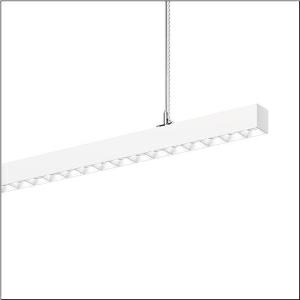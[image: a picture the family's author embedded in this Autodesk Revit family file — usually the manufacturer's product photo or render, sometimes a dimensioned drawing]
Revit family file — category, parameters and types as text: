
# Revit family: silica_r__21_51mx37da47wb_26de
name_source: partatom
category: Lighting Fixtures
units: mm (PartAtom-declared; Revit-internal decimal feet)

## family parameters
Cut with Voids When Loaded = No
Host = Face
Light Source = No
Part Type = Normal
Room Calculation Point = No
Round Connector Dimension = Use Diameter
Shared = No

## types (1)
- --- (1 x LED, 7300 lm, 44 W, 4000K)
    Apparent Load = 44 VA
    CIE Flux Codes = 71 92 99 59 100
    Color Rendering = 80
    Color Temperature = 4000K
    Default Elevation = 1800 mm
    Description = Silica® 21, office luminaire, primary light control with darklight reflector, of PMMA, white, CAT 2 (L<= 3000cd/m²), light emission: direct/indirect distribution, primary light characteristic: asymmetric, installation type: suspended mounting, LED, rated luminous flux: 7.300lm, luminous efficacy: 166lm/W, light colour: 840, colour temperature: 4000K, control gear: DALI 2, with terminal, 3+2-pole, max. 2.5mm², mains connection: 220..240V, AC, 50/60Hz, rated input power: 44W, luminaire housing, of aluminium, traffic white (RAL 9016), length: 1.204mm, width: 53mm, height: 53mm, protection rating (complete): IP20, insulation class (complete): insulation class I (protective earthing), certification: CE, permissible operating ambient temperature: 0..+35°C, standard: EN 50419, packaging unit: 1 piece
    Height = 53 mm
    Lamp = 1 x LED
    Lamp Light Flux = 7300 lm
    Lamp Power = 44 W
    Lamp count = 1
    Length = 1204 mm
    Luminous efficacy = 166 lm/W
    Manufacturer = Siteco
    ModVariant = No
    Model = 51MX37DA47WB
    Mounting Place = Ceiling
    Mounting Type = Pendant
    Number of Poles = 1
    OnlyDefault = Yes
    Power Factor = 1
    Product Name = Silica® 21
    Product group = office luminaire | ceiling pendant
    ProductGroupID = 903
    Protection Class = Protection class I
    Protection Degree = IP 20
    RLX_Detail_Level = 1
    RLX_Emergency_Light_Flux = 0 lm
    RLX_Emergency_Type = 0
    RLX_Emergency_Type_DB = No
    RlxData = <blob elided: 41801 chars, md5=945b49b5>
    Socket = socket
    Standby Power = 0 W
    System Light Flux = 7300 lm
    System Power = 44 W
    Type Comments = factory setting: luminous flux: 100 % | dim-lin: 254 | 368 mA
    Type Image = l_1335921.jpg
    URL = http://relux.com
    VarID = @adj_123623
    Voltage = 0 V
    Weight = 0.00 kg
    Width = 53 mm

## geometry (parser evidence)
native form markers: Blend x4, Sweep x11
no freeform markers — native parametric forms only
